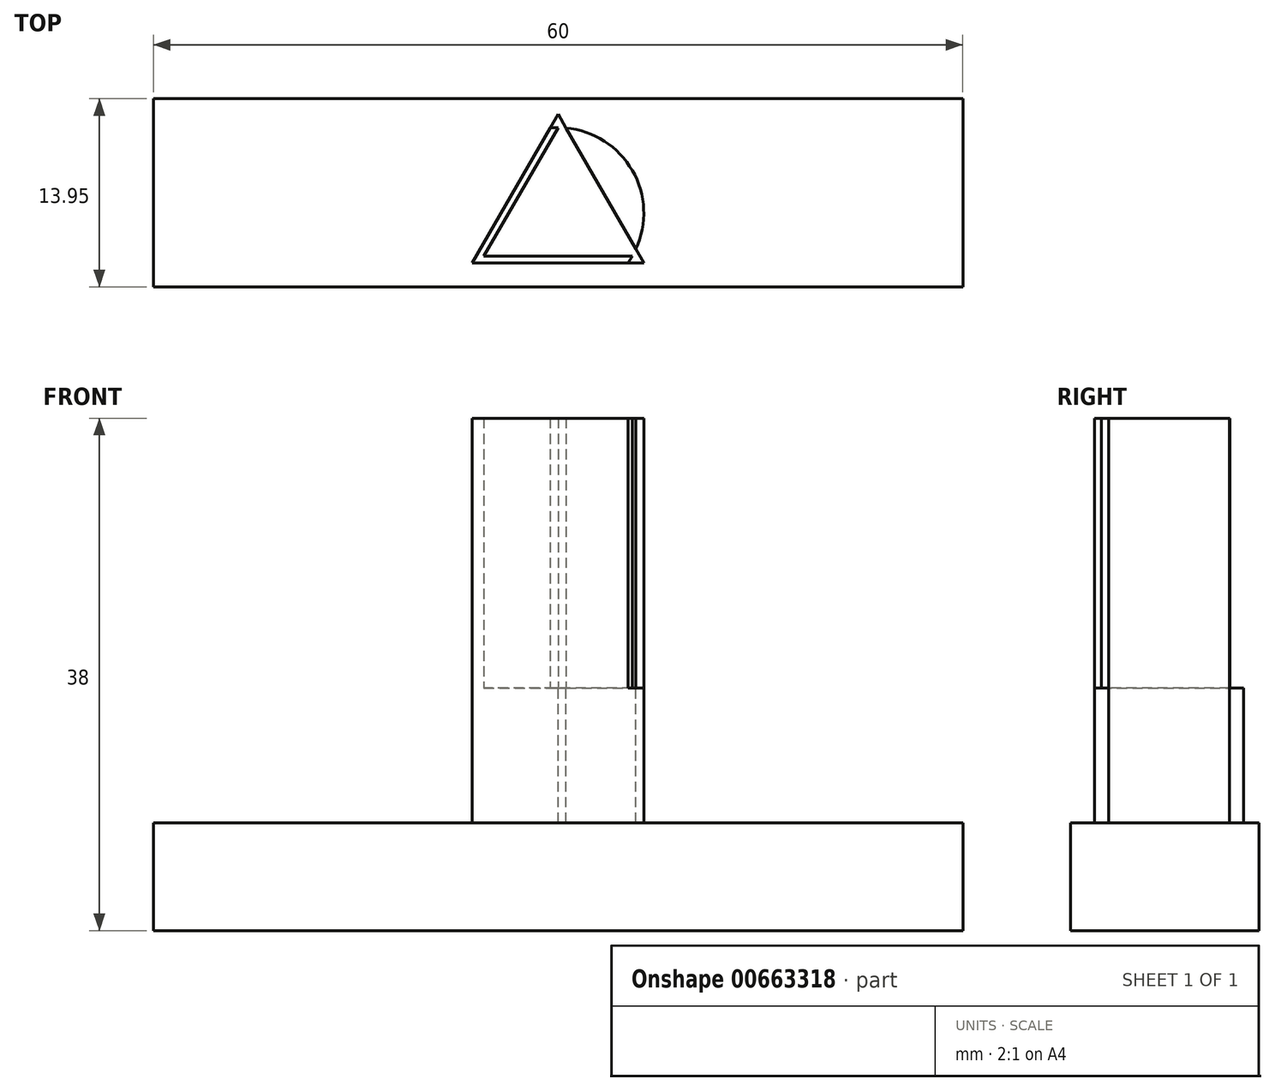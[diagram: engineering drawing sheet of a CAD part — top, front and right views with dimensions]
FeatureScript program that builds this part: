
annotation { "Feature Type Name" : "Feature", "Feature Type Description" : "" }
export const myFeature = defineFeature(function(context is Context, id is Id, definition is map)
    precondition{}
    {
        {
            var Q0;
            Q0=qCreatedBy(makeId("Top.planeOp"),FACE);
            var sketch = newSketch(context, id + "F0", { "sketchPlane" : qUnion([Q0])});
            skLineSegment(sketch, "E0", {"start": v(-15.1, 22.68) * mm, "end": v(-9.6, 32.2) * mm});
            skLineSegment(sketch, "E1", {"start": v(-9.6, 32.2) * mm, "end": v(-4.1, 22.68) * mm});
            skLineSegment(sketch, "E2", {"start": v(-4.1, 22.68) * mm, "end": v(-15.1, 22.68) * mm});
            skCircle(sketch, "E3", {"center": v(-9.6, 25.85) * mm, "radius": 6.35 * mm});
            skCircle(sketch, "E4", {"center": v(-9.6, 25.85) * mm, "radius": 8.5 * mm});
            skLineSegment(sketch, "E5", {"start": v(-21.84, 20.4) * mm, "end": v(-16.11, 20.4) * mm});
            skLineSegment(sketch, "E6", {"start": v(-16.11, 20.4) * mm, "end": v(-0.22, 20.4) * mm});
            skLineSegment(sketch, "E7.0", {"start": v(-15.96, 22.18) * mm, "end": v(-9.6, 33.2) * mm});
            skLineSegment(sketch, "E7.1", {"start": v(-3.23, 22.18) * mm, "end": v(-15.96, 22.18) * mm});
            skLineSegment(sketch, "E7.2", {"start": v(-9.6, 33.2) * mm, "end": v(-3.23, 22.18) * mm});
            skSolve(sketch);
        }
        {
            var Q0;
            {var subQ0=sQuery(id+"F0.wireOp",EDGE,"E7.0");var subQ1=sQuery(id+"F0.wireOp",EDGE,"E3");var subQ2=makeQuery(id+"F0.imprint","INTERSECT",VERTEX,{"disambiguationData":[OD(0.0)],"derivedFrom":[subQ1,subQ0]});Q0=makeQuery(id+"F0.imprint","IMPRINT",FACE,{"disambiguationData":[TD([[makeQuery(id+"F0.imprint","IMPRINT",EDGE,{"disambiguationData":[TD([[subQ2,-1.0]])],"derivedFrom":subQ1}),1.0]])]});}
            var Q1;
            {var subQ0=sQuery(id+"F0.wireOp",EDGE,"E7.2");var subQ1=sQuery(id+"F0.wireOp",EDGE,"E3");var subQ2=makeQuery(id+"F0.imprint","INTERSECT",VERTEX,{"disambiguationData":[OD(0.0)],"derivedFrom":[subQ1,subQ0]});Q1=makeQuery(id+"F0.imprint","IMPRINT",FACE,{"disambiguationData":[TD([[makeQuery(id+"F0.imprint","IMPRINT",EDGE,{"disambiguationData":[TD([[subQ2,1.0]])],"derivedFrom":subQ1}),1.0]])]});}
            var Q2;
            {var subQ3=sQuery(id+"F0.wireOp",EDGE,"E3");var subQ11=sQuery(id+"F0.wireOp",EDGE,"E7.0");var subQ12=makeQuery(id+"F0.imprint","INTERSECT",VERTEX,{"disambiguationData":[OD(0.0)],"derivedFrom":[subQ3,subQ11]});Q2=makeQuery(id+"F0.imprint","IMPRINT",FACE,{"disambiguationData":[TD([[makeQuery(id+"F0.imprint","IMPRINT",EDGE,{"disambiguationData":[TD([[subQ12,-1.0]])],"derivedFrom":subQ3}),-1.0]])]});}
            var Q3;
            {var subQ0=sQuery(id+"F0.wireOp",EDGE,"E7.1");var subQ1=sQuery(id+"F0.wireOp",EDGE,"E3");var subQ2=makeQuery(id+"F0.imprint","INTERSECT",VERTEX,{"disambiguationData":[OD(0.0)],"derivedFrom":[subQ1,subQ0]});Q3=makeQuery(id+"F0.imprint","IMPRINT",FACE,{"disambiguationData":[TD([[makeQuery(id+"F0.imprint","IMPRINT",EDGE,{"disambiguationData":[TD([[subQ2,-1.0]])],"derivedFrom":subQ1}),1.0]])]});}
            extrude(context, id + "F1", {"entities" : qUnion([Q0, Q1, Q2, Q3]), "depth" : 20 * mm, "offsetDistance" : 25 * mm});
        }
        {
            var Q0;
            Q0=qCreatedBy(makeId("Top.planeOp"),FACE);
            var sketch = newSketch(context, id + "F2", { "sketchPlane" : qUnion([Q0])});
            skLineSegment(sketch, "E8.bottom", {"start": v(20.4, 34.35) * mm, "end": v(-39.6, 34.35) * mm});
            skLineSegment(sketch, "E8.top", {"start": v(20.4, 20.4) * mm, "end": v(-39.6, 20.4) * mm});
            skLineSegment(sketch, "E8.left", {"start": v(20.4, 34.35) * mm, "end": v(20.4, 20.4) * mm});
            skLineSegment(sketch, "E8.right", {"start": v(-39.6, 34.35) * mm, "end": v(-39.6, 20.4) * mm});
            skSolve(sketch);
        }
        {
            var Q0;
            {var subQ0=sQuery(id+"F0.wireOp",EDGE,"E7.0");var subQ1=sQuery(id+"F0.wireOp",EDGE,"E3");var subQ2=makeQuery(id+"F0.imprint","INTERSECT",VERTEX,{"disambiguationData":[OD(0.0)],"derivedFrom":[subQ1,subQ0]});Q0=makeQuery(id+"F0.imprint","IMPRINT",FACE,{"disambiguationData":[TD([[makeQuery(id+"F0.imprint","IMPRINT",EDGE,{"disambiguationData":[TD([[subQ2,-1.0]])],"derivedFrom":subQ1}),1.0]])]});}
            var Q1;
            Q1=makeQuery(id+"F0.imprint","IMPRINT",FACE,{"disambiguationData":[TD([[makeQuery(id+"F0.imprint","IMPRINT",EDGE,{"derivedFrom":sQuery(id+"F0.wireOp",EDGE,"E0")}),-1.0]])]});
            var Q2;
            {var subQ2=sQuery(id+"F0.wireOp",EDGE,"E7.2");var subQ4=sQuery(id+"F0.wireOp",EDGE,"E7.0");var subQ6=makeQuery(id+"F0.imprint","INTERSECT",VERTEX,{"derivedFrom":[subQ4,subQ2]});Q2=makeQuery(id+"F0.imprint","IMPRINT",FACE,{"disambiguationData":[TD([[makeQuery(id+"F0.imprint","IMPRINT",EDGE,{"disambiguationData":[TD([[subQ6,1.0]])],"derivedFrom":subQ4}),-1.0]])]});}
            var Q3;
            {var subQ0=sQuery(id+"F0.wireOp",EDGE,"E0");Q3=makeQuery(id+"F0.imprint","IMPRINT",FACE,{"disambiguationData":[TD([[makeQuery(id+"F0.imprint","IMPRINT",EDGE,{"derivedFrom":subQ0}),1.0]])]});}
            var Q4;
            {var subQ2=sQuery(id+"F0.wireOp",EDGE,"E7.0");var subQ4=sQuery(id+"F0.wireOp",EDGE,"E7.1");var subQ6=makeQuery(id+"F0.imprint","INTERSECT",VERTEX,{"derivedFrom":[subQ2,subQ4]});Q4=makeQuery(id+"F0.imprint","IMPRINT",FACE,{"disambiguationData":[TD([[makeQuery(id+"F0.imprint","IMPRINT",EDGE,{"disambiguationData":[TD([[subQ6,-1.0]])],"derivedFrom":subQ2}),-1.0]])]});}
            var Q5;
            {var subQ3=sQuery(id+"F0.wireOp",EDGE,"E3");var subQ11=sQuery(id+"F0.wireOp",EDGE,"E7.0");var subQ12=makeQuery(id+"F0.imprint","INTERSECT",VERTEX,{"disambiguationData":[OD(0.0)],"derivedFrom":[subQ3,subQ11]});Q5=makeQuery(id+"F0.imprint","IMPRINT",FACE,{"disambiguationData":[TD([[makeQuery(id+"F0.imprint","IMPRINT",EDGE,{"disambiguationData":[TD([[subQ12,-1.0]])],"derivedFrom":subQ3}),-1.0]])]});}
            var Q6;
            {var subQ0=sQuery(id+"F0.wireOp",EDGE,"E7.1");var subQ1=sQuery(id+"F0.wireOp",EDGE,"E3");var subQ2=makeQuery(id+"F0.imprint","INTERSECT",VERTEX,{"disambiguationData":[OD(0.0)],"derivedFrom":[subQ1,subQ0]});Q6=makeQuery(id+"F0.imprint","IMPRINT",FACE,{"disambiguationData":[TD([[makeQuery(id+"F0.imprint","IMPRINT",EDGE,{"disambiguationData":[TD([[subQ2,-1.0]])],"derivedFrom":subQ1}),1.0]])]});}
            var Q7;
            {var subQ0=sQuery(id+"F0.wireOp",EDGE,"E7.2");var subQ1=sQuery(id+"F0.wireOp",EDGE,"E3");var subQ2=makeQuery(id+"F0.imprint","INTERSECT",VERTEX,{"disambiguationData":[OD(0.0)],"derivedFrom":[subQ1,subQ0]});Q7=makeQuery(id+"F0.imprint","IMPRINT",FACE,{"disambiguationData":[TD([[makeQuery(id+"F0.imprint","IMPRINT",EDGE,{"disambiguationData":[TD([[subQ2,1.0]])],"derivedFrom":subQ1}),1.0]])]});}
            var Q8;
            {var subQ0=sQuery(id+"F0.wireOp",EDGE,"E1");Q8=makeQuery(id+"F0.imprint","IMPRINT",FACE,{"disambiguationData":[TD([[makeQuery(id+"F0.imprint","IMPRINT",EDGE,{"derivedFrom":subQ0}),1.0]])]});}
            var Q9;
            {var subQ0=sQuery(id+"F0.wireOp",EDGE,"E2");Q9=makeQuery(id+"F0.imprint","IMPRINT",FACE,{"disambiguationData":[TD([[makeQuery(id+"F0.imprint","IMPRINT",EDGE,{"derivedFrom":subQ0}),1.0]])]});}
            var Q10;
            {var subQ2=sQuery(id+"F0.wireOp",EDGE,"E7.1");var subQ4=sQuery(id+"F0.wireOp",EDGE,"E7.2");var subQ6=makeQuery(id+"F0.imprint","INTERSECT",VERTEX,{"derivedFrom":[subQ2,subQ4]});Q10=makeQuery(id+"F0.imprint","IMPRINT",FACE,{"disambiguationData":[TD([[makeQuery(id+"F0.imprint","IMPRINT",EDGE,{"disambiguationData":[TD([[subQ6,-1.0]])],"derivedFrom":subQ2}),-1.0]])]});}
            extrude(context, id + "F3", {"entities" : qUnion([Q0, Q1, Q2, Q3, Q4, Q5, Q6, Q7, Q8, Q9, Q10]), "operationType" : NewBodyOperationType.ADD, "oppositeDirection" : true, "depth" : 10 * mm, "offsetDistance" : 25 * mm});
        }
        {
            var Q0;
            Q0 = qSketchRegion(id + "F2", true);
            extrude(context, id + "F4", {"entities" : qUnion([Q0]), "operationType" : NewBodyOperationType.ADD, "oppositeDirection" : true, "depth" : 18 * mm, "offsetDistance" : 25 * mm, "hasSecondDirection" : true, "secondDirectionOppositeDirection" : true, "secondDirectionDepth" : 10 * mm});
        }
    });
